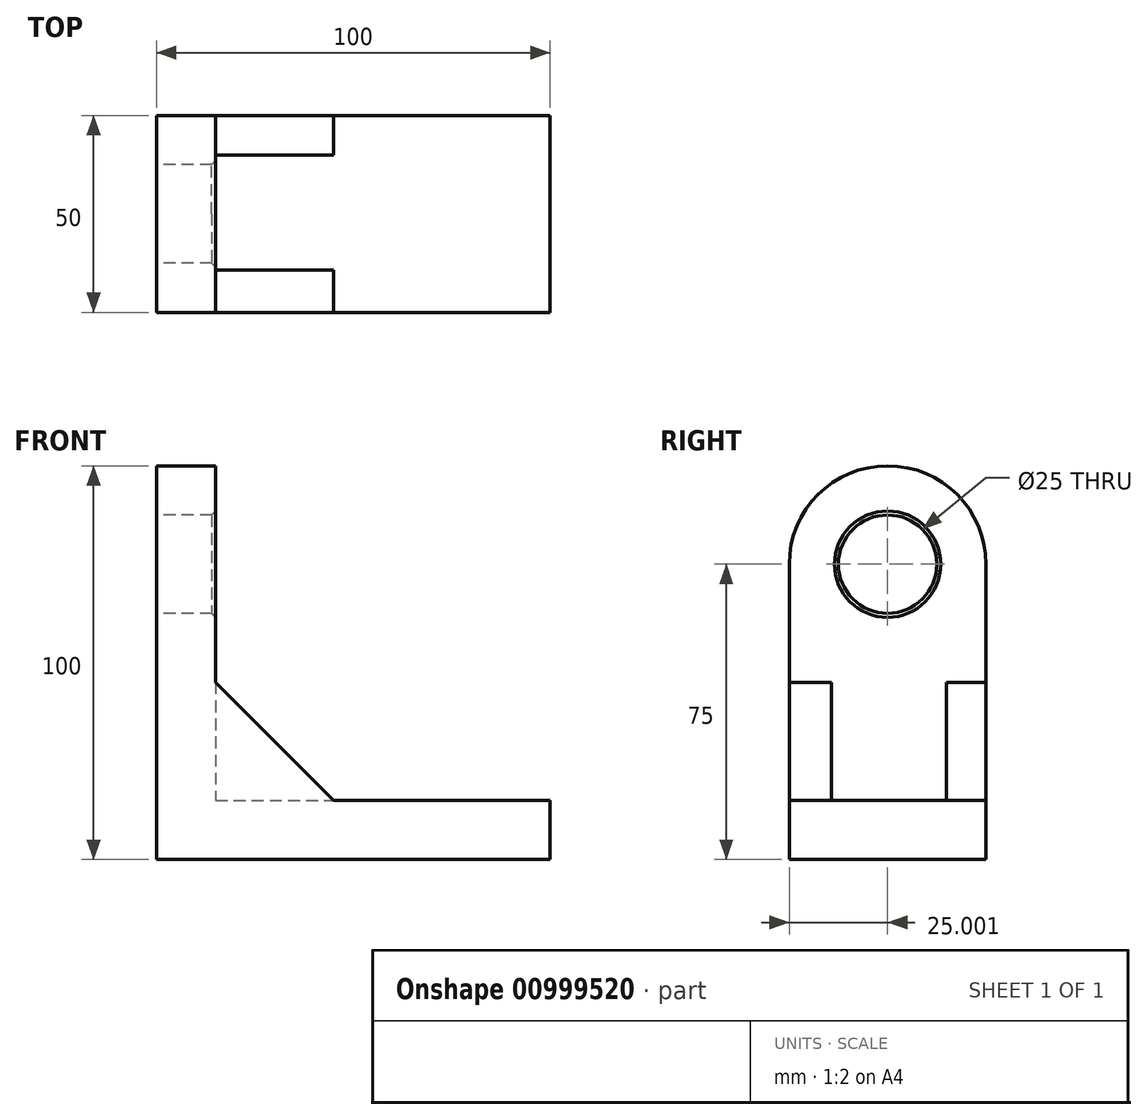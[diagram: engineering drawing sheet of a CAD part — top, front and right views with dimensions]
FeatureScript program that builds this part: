
annotation { "Feature Type Name" : "Feature", "Feature Type Description" : "" }
export const myFeature = defineFeature(function(context is Context, id is Id, definition is map)
    precondition{}
    {
        {
            var Q0;
            Q0=qCreatedBy(makeId("Top.planeOp"),FACE);
            var sketch = newSketch(context, id + "F0", { "sketchPlane" : qUnion([Q0])});
            skLineSegment(sketch, "E0.bottom", {"start": v(-48.79, 16.15) * mm, "end": v(51.21, 16.15) * mm});
            skLineSegment(sketch, "E0.top", {"start": v(-48.79, -33.85) * mm, "end": v(51.21, -33.85) * mm});
            skLineSegment(sketch, "E0.left", {"start": v(-48.79, 16.15) * mm, "end": v(-48.79, -33.85) * mm});
            skLineSegment(sketch, "E0.right", {"start": v(51.21, 16.15) * mm, "end": v(51.21, -33.85) * mm});
            skSolve(sketch);
        }
        {
            var Q0;
            Q0=makeQuery(id+"F0.imprint","IMPRINT",FACE,{"disambiguationData":[TD([[makeQuery(id+"F0.imprint","IMPRINT",EDGE,{"derivedFrom":sQuery(id+"F0.wireOp",EDGE,"E0.bottom")}),-1.0]])]});
            extrude(context, id + "F1", {"entities" : qUnion([Q0]), "depth" : 15 * mm, "offsetDistance" : 25 * mm});
        }
        {
            var Q0;
            Q0=makeQuery(id+"F1.opExtrude","CAP_FACE",FACE,{"disambiguationData":[OSD([sQuery(id+"F0.wireOp",EDGE,"E0.bottom"),sQuery(id+"F0.wireOp",EDGE,"E0.top"),sQuery(id+"F0.wireOp",EDGE,"E0.left"),sQuery(id+"F0.wireOp",EDGE,"E0.right")])],"isStart":false});
            var sketch = newSketch(context, id + "F2", { "sketchPlane" : qUnion([Q0])});
            skLineSegment(sketch, "E1.bottom", {"start": v(-48.79, 16.15) * mm, "end": v(-33.79, 16.15) * mm});
            skLineSegment(sketch, "E1.top", {"start": v(-48.79, -33.85) * mm, "end": v(-33.79, -33.85) * mm});
            skLineSegment(sketch, "E1.left", {"start": v(-48.79, 16.15) * mm, "end": v(-48.79, -33.85) * mm});
            skLineSegment(sketch, "E1.right", {"start": v(-33.79, 16.15) * mm, "end": v(-33.79, -33.85) * mm});
            skSolve(sketch);
        }
        {
            var Q0;
            Q0=makeQuery(id+"F2.imprint","IMPRINT",FACE,{"disambiguationData":[TD([[makeQuery(id+"F2.imprint","IMPRINT",EDGE,{"derivedFrom":sQuery(id+"F2.wireOp",EDGE,"E1.bottom")}),-1.0]])]});
            extrude(context, id + "F3", {"entities" : qUnion([Q0]), "operationType" : NewBodyOperationType.ADD, "depth" : 85 * mm, "offsetDistance" : 25 * mm});
        }
        {
            var Q0;
            Q0=makeQuery(id+"F1.opExtrude","CAP_FACE",FACE,{"disambiguationData":[OSD([sQuery(id+"F0.wireOp",EDGE,"E0.bottom"),sQuery(id+"F0.wireOp",EDGE,"E0.top"),sQuery(id+"F0.wireOp",EDGE,"E0.left"),sQuery(id+"F0.wireOp",EDGE,"E0.right")])],"isStart":false});
            var sketch = newSketch(context, id + "F4", { "sketchPlane" : qUnion([Q0])});
            skLineSegment(sketch, "E2.bottom", {"start": v(-33.79, -33.85) * mm, "end": v(-3.79, -33.85) * mm});
            skLineSegment(sketch, "E2.top", {"start": v(-33.79, -23.06) * mm, "end": v(-3.79, -23.06) * mm});
            skLineSegment(sketch, "E2.left", {"start": v(-33.79, -33.85) * mm, "end": v(-33.79, -23.06) * mm});
            skLineSegment(sketch, "E2.right", {"start": v(-3.79, -33.85) * mm, "end": v(-3.79, -23.06) * mm});
            skLineSegment(sketch, "E3.bottom", {"start": v(-33.79, 16.15) * mm, "end": v(-3.79, 16.15) * mm});
            skLineSegment(sketch, "E3.top", {"start": v(-33.79, 6.15) * mm, "end": v(-3.79, 6.15) * mm});
            skLineSegment(sketch, "E3.left", {"start": v(-33.79, 16.15) * mm, "end": v(-33.79, 6.15) * mm});
            skLineSegment(sketch, "E3.right", {"start": v(-3.79, 16.15) * mm, "end": v(-3.79, 6.15) * mm});
            skSolve(sketch);
        }
        {
            var Q0;
            Q0=makeQuery(id+"F4.imprint","IMPRINT",FACE,{"disambiguationData":[TD([[makeQuery(id+"F4.imprint","IMPRINT",EDGE,{"derivedFrom":sQuery(id+"F4.wireOp",EDGE,"E2.bottom")}),1.0]])]});
            var Q1;
            Q1=makeQuery(id+"F4.imprint","IMPRINT",FACE,{"disambiguationData":[TD([[makeQuery(id+"F4.imprint","IMPRINT",EDGE,{"derivedFrom":sQuery(id+"F4.wireOp",EDGE,"E3.bottom")}),-1.0]])]});
            extrude(context, id + "F5", {"entities" : qUnion([Q0, Q1]), "operationType" : NewBodyOperationType.ADD, "depth" : 30 * mm, "offsetDistance" : 25 * mm});
        }
        {
            var Q0;
            Q0=makeQuery(id+"F5.opExtrude","CAP_EDGE",EDGE,{"disambiguationData":[OSD([sQuery(id+"F4.wireOp",EDGE,"E3.right")])],"isStart":false});
            var Q1;
            Q1=makeQuery(id+"F5.opExtrude","CAP_EDGE",EDGE,{"disambiguationData":[OSD([sQuery(id+"F4.wireOp",EDGE,"E2.right")])],"isStart":false});
            chamfer(context, id + "F6", {"entities" : qUnion([Q0, Q1]), "width" : 30 * mm, "tangentPropagation" : true});
        }
        {
            var Q0;
            Q0=makeQuery(id+"F3.boolean.opBoolean","MERGE",FACE,{"derivedFrom":[makeQuery(id+"F1.opExtrude","SWEPT_FACE",FACE,{"disambiguationData":[OSD([sQuery(id+"F0.wireOp",EDGE,"E0.left")])]}),makeQuery(id+"F3.opExtrude","SWEPT_FACE",FACE,{"disambiguationData":[OSD([sQuery(id+"F2.wireOp",EDGE,"E1.left")])]})]});
            var sketch = newSketch(context, id + "F7", { "sketchPlane" : qUnion([Q0])});
            skCircle(sketch, "E4", {"center": v(8.85, 75) * mm, "radius": 12.5 * mm});
            skSolve(sketch);
        }
        {
            var Q0;
            Q0 = qSketchRegion(id + "F7", true);
            var sketch = newSketch(context, id + "F8", { "sketchPlane" : qUnion([Q0])});
            skSolve(sketch);
        }
        {
            var Q0;
            Q0 = qSketchRegion(id + "F7", true);
            var Q1;
            Q1=makeQuery(id+"F8.imprint","IMPRINT",FACE,{"disambiguationData":[TD([[makeQuery(id+"F8.imprint","IMPRINT",EDGE,{"derivedFrom":makeQuery(id+"F7.imprint","IMPRINT",EDGE,{"derivedFrom":sQuery(id+"F7.wireOp",EDGE,"E4")})}),1.0]])]});
            extrude(context, id + "F9", {"entities" : qUnion([Q0, Q1]), "operationType" : NewBodyOperationType.REMOVE, "oppositeDirection" : true, "depth" : 25 * mm, "offsetDistance" : 25 * mm});
        }
        {
            var Q0;
            Q0=makeQuery(id+"F3.opExtrude","CAP_EDGE",EDGE,{"disambiguationData":[OSD([sQuery(id+"F2.wireOp",EDGE,"E1.bottom")])],"isStart":false});
            var Q1;
            Q1=makeQuery(id+"F3.opExtrude","CAP_EDGE",EDGE,{"disambiguationData":[OSD([sQuery(id+"F2.wireOp",EDGE,"E1.top")])],"isStart":false});
            fillet(context, id + "F10", {"entities" : qUnion([Q0, Q1]), "radius" : 25 * mm, "tangentPropagation" : true, "allowEdgeOverflow" : false});
        }
        {
            var Q0;
            {var subQ0=sQuery(id+"F7.wireOp",EDGE,"E4");Q0=makeQuery(id+"F9.boolean.opBoolean","INTERSECT",EDGE,{"derivedFrom":[makeQuery(id+"F3.opExtrude","SWEPT_FACE",FACE,{"disambiguationData":[OSD([sQuery(id+"F2.wireOp",EDGE,"E1.right")])]}),makeQuery(id+"F9.opExtrude","SWEPT_FACE",FACE,{"disambiguationData":[OSD([subQ0]),TDD([makeQuery(id+"F7.imprint","IMPRINT",EDGE,{"derivedFrom":subQ0})])]})]});}
            var Q1;
            {var subQ0=sQuery(id+"F7.wireOp",EDGE,"E4");Q1=makeQuery(id+"F9.boolean.opBoolean","COPY",EDGE,{"derivedFrom":makeQuery(id+"F9.opExtrude","CAP_EDGE",EDGE,{"disambiguationData":[OSD([subQ0]),TDD([makeQuery(id+"F7.imprint","IMPRINT",EDGE,{"derivedFrom":subQ0})])],"isStart":true})});}
            chamfer(context, id + "F11", {"entities" : qUnion([Q0, Q1]), "width" : 1 * mm, "tangentPropagation" : true});
        }
    });
